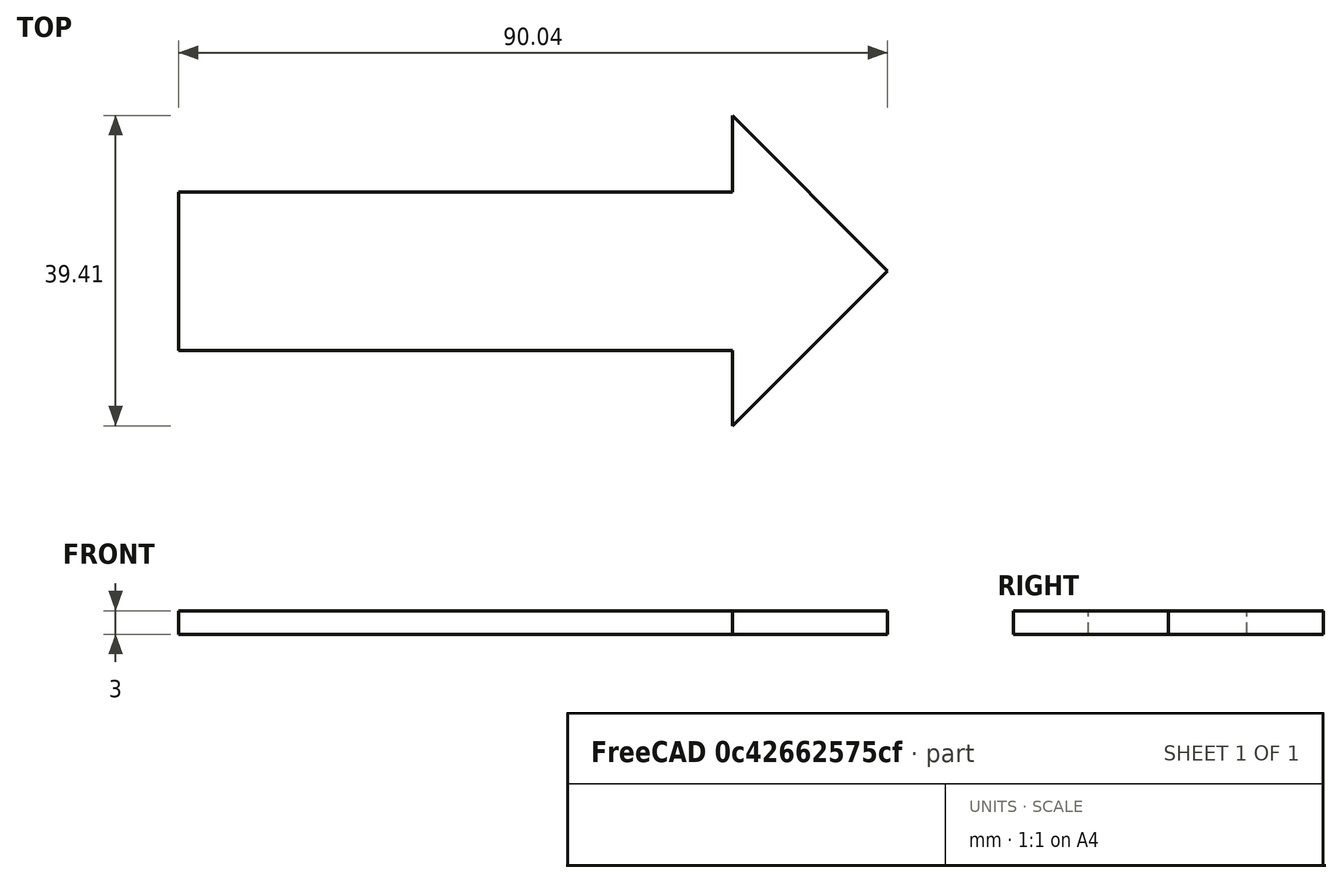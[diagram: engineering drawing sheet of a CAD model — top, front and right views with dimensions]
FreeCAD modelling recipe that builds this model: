
FCSTD DOCUMENT  (FreeCAD 0.21R33694 (Git))
Label: OJT1_T16R02_fletxa
License: All rights reserved
LicenseURL: https://en.wikipedia.org/wiki/All_rights_reserved
objects: Sketcher::SketchObject×1, PartDesign::Pad×1, PartDesign::Body×1
note: 4 computed .brp shape members not serialized (recipe doc carries the construction recipe); baked Part::Feature solids carry a one-line shape summary decoded from their .brp

FEATURE [Sketcher::SketchObject] Sketch  label="fletxa"
  FullyConstrained = false
  MapMode = 5
  Support = -> [XY_Plane]
  sketch-geometry (7):
    g0: LineSegment StartX=-30.1843 StartY=-10.1464 StartZ=0 EndX=-30.1843 EndY=9.98067 EndZ=0
    g1: LineSegment StartX=-30.1843 StartY=9.98067 StartZ=0 EndX=40.1547 EndY=9.98067 EndZ=0
    g2: LineSegment StartX=40.1547 StartY=9.98067 StartZ=0 EndX=40.1547 EndY=19.7264 EndZ=0
    g3: LineSegment StartX=40.1547 StartY=19.7264 StartZ=0 EndX=59.858 EndY=0 EndZ=0
    g4: LineSegment StartX=59.858 StartY=0 StartZ=0 EndX=40.1547 EndY=-19.6804 EndZ=0
    g5: LineSegment StartX=40.1547 StartY=-19.6804 StartZ=0 EndX=40.1547 EndY=-10.1464 EndZ=0
    g6: LineSegment StartX=40.1547 StartY=-10.1464 StartZ=0 EndX=-30.1843 EndY=-10.1464 EndZ=0
  constraints (13):
    c: Vertical(g0)
    c: Coincident(g0,g1)
    c: Horizontal(g1)
    c: Coincident(g1,g2)
    c: Vertical(g2)
    c: Coincident(g2,g3)
    c: PointOnObject(g3,g-1)
    c: Coincident(g3,g4)
    c: Coincident(g4,g5)
    c: Vertical(g5)
    c: Coincident(g5,g6)
    c: Coincident(g6,g0)
    c: Horizontal(g6)
FEATURE [PartDesign::Pad] Pad  label="FLETXA"
  Direction = (0,0,1)
  Length = 3
  Length2 = 10
  Profile = -> Sketch
  ReferenceAxis = -> Sketch [N_Axis]
  Type = 0
FEATURE [PartDesign::Body] Body
  Group = -> [Sketch,Pad]
  Origin = -> Origin
  Tip = -> Pad
